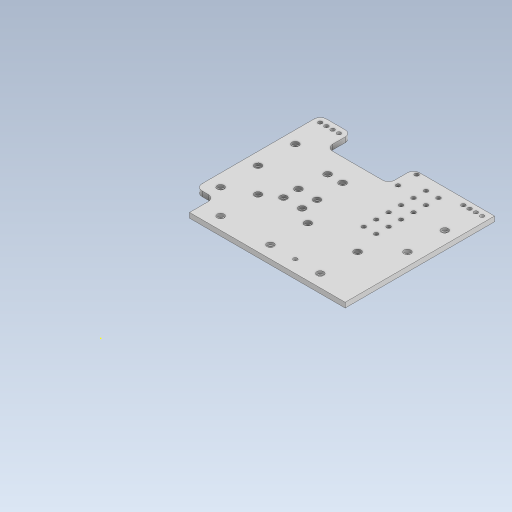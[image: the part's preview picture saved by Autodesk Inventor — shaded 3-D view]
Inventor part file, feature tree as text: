
AUTODESK INVENTOR PART (.ipt)
format: ipt  version: 2023.5 (Build 275446000, 446)  size: 519,680 bytes
history: native  units: in
note: dims shown in document units (in); Inventor stores cm internally (conversion verified against a paired STEP export)
features: sketch x2, extrude x2, fillet x1
ambient origin geometry x8: Origin, YZ Plane, XZ Plane, XY Plane, X Axis, Y Axis, Z Axis, Center Point
bodies: Solid1 (feature_tree)
feature tree (5):
  sketch  "Sketch1"  dims[d29=0.1575in d30=0.0in d31=0.0787in d32=0.0in]
  extrude  "Extrusion1"  Depth=0.0787in TaperAngle=0.0deg
  sketch  "Sketch2"  dims[d33=5.5118in d34=4.7244in d35=0.3937in d36=0.3937in d37=0.3937in d39=0.3937in d40=0.3937in d41=0.3937in d42=0.3937in d43=0.3937in d44=1.5748in d45=1.5748in d46=0.126in d47=0.0984in d48=0.1969in d49=0.126in d50=0.5906in d60=0.126in d61=0.126in d63=0.126in d65=0.126in d66=0.3937in d69=0.3937in d70=0.3937in d71=0.3937in d76=0.1299in d77=0.2165in d78=1.1811in d79=0.1299in d80=0.2165in d81=0.5906in d82=0.7874in d83=0.1969in d84=0.126in d85=0.7874in]
  extrude  "Extrusion2"  Depth=4.7244in
  fillet  "Fillet1"  Radius=0.3937in
